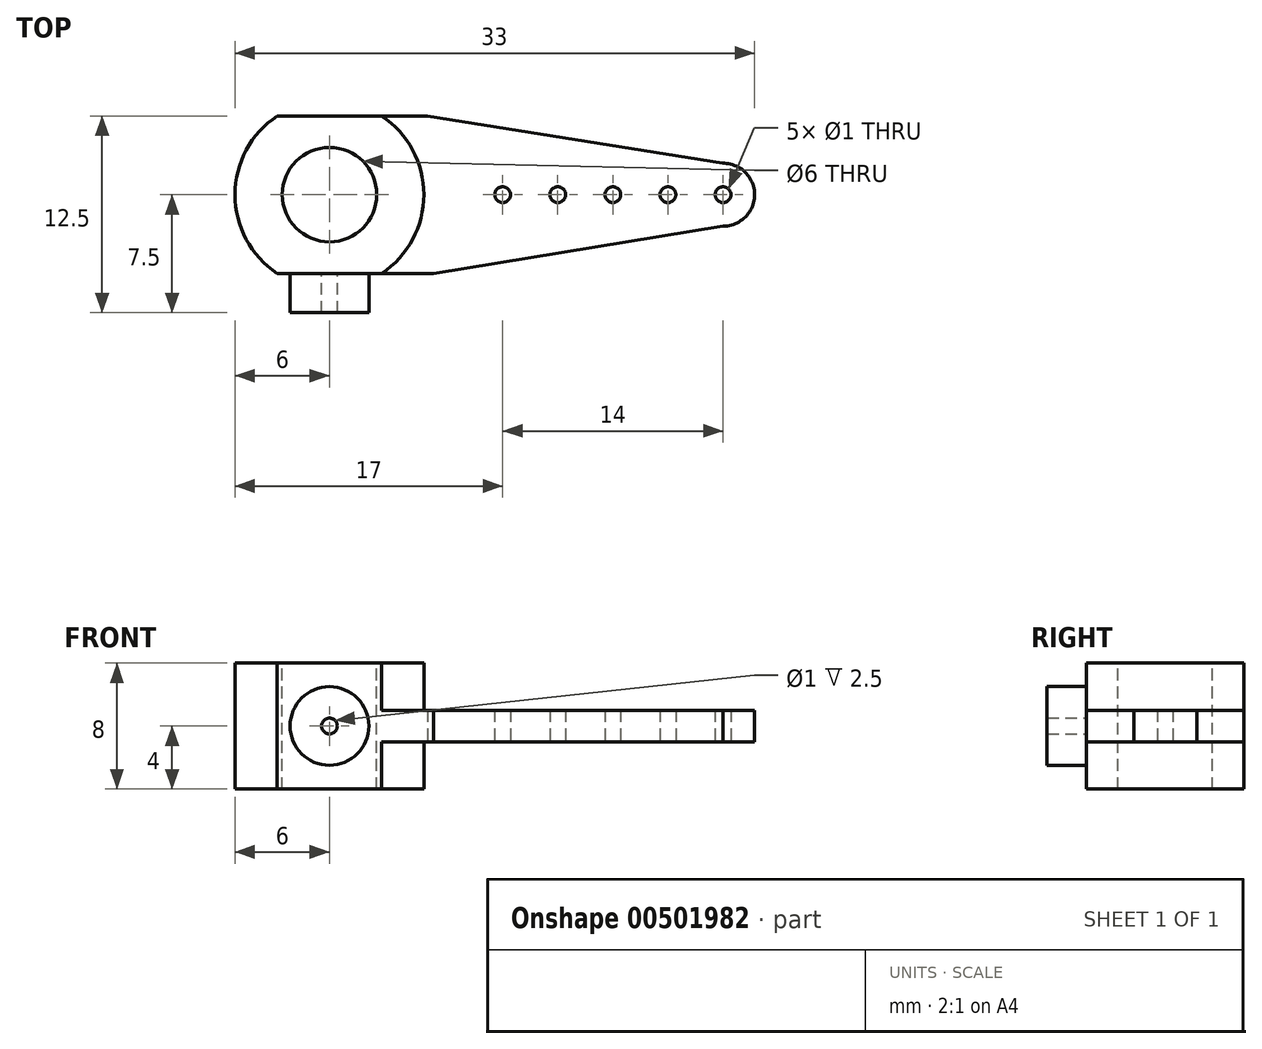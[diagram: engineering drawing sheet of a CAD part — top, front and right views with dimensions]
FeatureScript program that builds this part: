
annotation { "Feature Type Name" : "Feature", "Feature Type Description" : "" }
export const myFeature = defineFeature(function(context is Context, id is Id, definition is map)
    precondition{}
    {
        {
            var Q0;
            Q0=qCreatedBy(makeId("Top.planeOp"),FACE);
            var sketch = newSketch(context, id + "F0", { "sketchPlane" : qUnion([Q0])});
            skCircle(sketch, "E0", {"center": v(0, 0) * mm, "radius": 3 * mm});
            skCircle(sketch, "E1", {"center": v(0, 0) * mm, "radius": 6 * mm, "construction": true});
            skLineSegment(sketch, "E2", {"start": v(0, 0) * mm, "end": v(25, 0) * mm, "construction": true});
            skCircle(sketch, "E3", {"center": v(25, 0) * mm, "radius": 2 * mm, "construction": true});
            skLineSegment(sketch, "E4", {"start": v(0, 6) * mm, "end": v(24.96, 2) * mm, "construction": true});
            skLineSegment(sketch, "E5", {"start": v(25, 0) * mm, "end": v(25, -2) * mm, "construction": true});
            skLineSegment(sketch, "E6", {"start": v(25, -2) * mm, "end": v(0, -6.08) * mm, "construction": true});
            skPoint(sketch, "E7", {"position": v(21.5, 0) * mm});
            skPoint(sketch, "E8", {"position": v(18, 0) * mm});
            skPoint(sketch, "E9", {"position": v(14.5, 0) * mm});
            skPoint(sketch, "E10", {"position": v(11, 0) * mm});
            skLineSegment(sketch, "E11", {"start": v(21.5, 0) * mm, "end": v(18, 0) * mm, "construction": true});
            skLineSegment(sketch, "E12", {"start": v(18, 0) * mm, "end": v(14.5, 0) * mm, "construction": true});
            skLineSegment(sketch, "E13", {"start": v(14.5, 0) * mm, "end": v(11, 0) * mm, "construction": true});
            skCircle(sketch, "E14", {"center": v(11, 0) * mm, "radius": 0.5 * mm});
            skCircle(sketch, "E15", {"center": v(14.5, 0) * mm, "radius": 0.5 * mm});
            skCircle(sketch, "E16", {"center": v(18, 0) * mm, "radius": 0.5 * mm});
            skCircle(sketch, "E17", {"center": v(21.5, 0) * mm, "radius": 0.5 * mm});
            skCircle(sketch, "E18", {"center": v(25, 0) * mm, "radius": 0.5 * mm});
            skLineSegment(sketch, "E19", {"start": v(0, 0) * mm, "end": v(0, -5) * mm});
            skLineSegment(sketch, "E20", {"start": v(0, 0) * mm, "end": v(0, 5) * mm, "construction": true});
            skLineSegment(sketch, "E21", {"start": v(0, 5) * mm, "end": v(8.07, 5) * mm, "construction": true});
            skLineSegment(sketch, "E22", {"start": v(8.07, 5) * mm, "end": v(-4.4, 5) * mm, "construction": true});
            skLineSegment(sketch, "E23", {"start": v(0, -5) * mm, "end": v(8.7, -5) * mm, "construction": true});
            skLineSegment(sketch, "E24", {"start": v(8.7, -5) * mm, "end": v(-5.37, -5) * mm, "construction": true});
            skArc(sketch, "E25", {"start": v(-3.32, -5) * mm, "mid": v(-6, 0) * mm, "end": v(-3.32, 5) * mm});
            skArc(sketch, "E26", {"start": v(24.96, 2) * mm, "mid": v(27, 0.02) * mm, "end": v(25, -2) * mm});
            skLineSegment(sketch, "E27", {"start": v(-3.32, 5) * mm, "end": v(6.24, 5) * mm});
            skLineSegment(sketch, "E28", {"start": v(6.24, 5) * mm, "end": v(24.96, 2) * mm});
            skLineSegment(sketch, "E29", {"start": v(25, -2) * mm, "end": v(6.61, -5) * mm});
            skLineSegment(sketch, "E30", {"start": v(6.61, -5) * mm, "end": v(-3.32, -5) * mm});
            skArc(sketch, "E31", {"start": v(3.32, 5) * mm, "mid": v(6, 0) * mm, "end": v(3.32, -5) * mm});
            skSolve(sketch);
        }
        {
            var Q0;
            Q0=makeQuery(id+"F0.imprint","IMPRINT",FACE,{"disambiguationData":[TD([[makeQuery(id+"F0.imprint","IMPRINT",EDGE,{"derivedFrom":sQuery(id+"F0.wireOp",EDGE,"E0")}),-1.0]])]});
            extrude(context, id + "F1", {"entities" : qUnion([Q0]), "oppositeDirection" : true, "depth" : 8 * mm, "symmetric" : true});
        }
        {
            var Q0;
            Q0=makeQuery(id+"F0.imprint","IMPRINT",FACE,{"disambiguationData":[TD([[makeQuery(id+"F0.imprint","IMPRINT",EDGE,{"derivedFrom":sQuery(id+"F0.wireOp",EDGE,"E14")}),-1.0]])]});
            extrude(context, id + "F2", {"entities" : qUnion([Q0]), "operationType" : NewBodyOperationType.ADD, "depth" : 2 * mm, "symmetric" : true});
        }
        {
            var Q0;
            {var subQ0=sQuery(id+"F0.wireOp",EDGE,"E30");Q0=makeQuery(id+"F2.boolean.opBoolean","MERGE",FACE,{"derivedFrom":[makeQuery(id+"F1.opExtrude","SWEPT_FACE",FACE,{"disambiguationData":[OSD([subQ0])]}),makeQuery(id+"F2.opExtrude","SWEPT_FACE",FACE,{"disambiguationData":[OSD([subQ0])]})]});}
            var sketch = newSketch(context, id + "F3", { "sketchPlane" : qUnion([Q0])});
            skCircle(sketch, "E32", {"center": v(0, 0) * mm, "radius": 2.5 * mm});
            skCircle(sketch, "E33", {"center": v(0, 0) * mm, "radius": 0.5 * mm});
            skSolve(sketch);
        }
        {
            var Q0;
            Q0=makeQuery(id+"F3.imprint","IMPRINT",FACE,{"disambiguationData":[TD([[makeQuery(id+"F3.imprint","IMPRINT",EDGE,{"derivedFrom":sQuery(id+"F3.wireOp",EDGE,"E32")}),1.0]])]});
            extrude(context, id + "F4", {"entities" : qUnion([Q0]), "operationType" : NewBodyOperationType.ADD, "depth" : 2.5 * mm});
        }
    });
